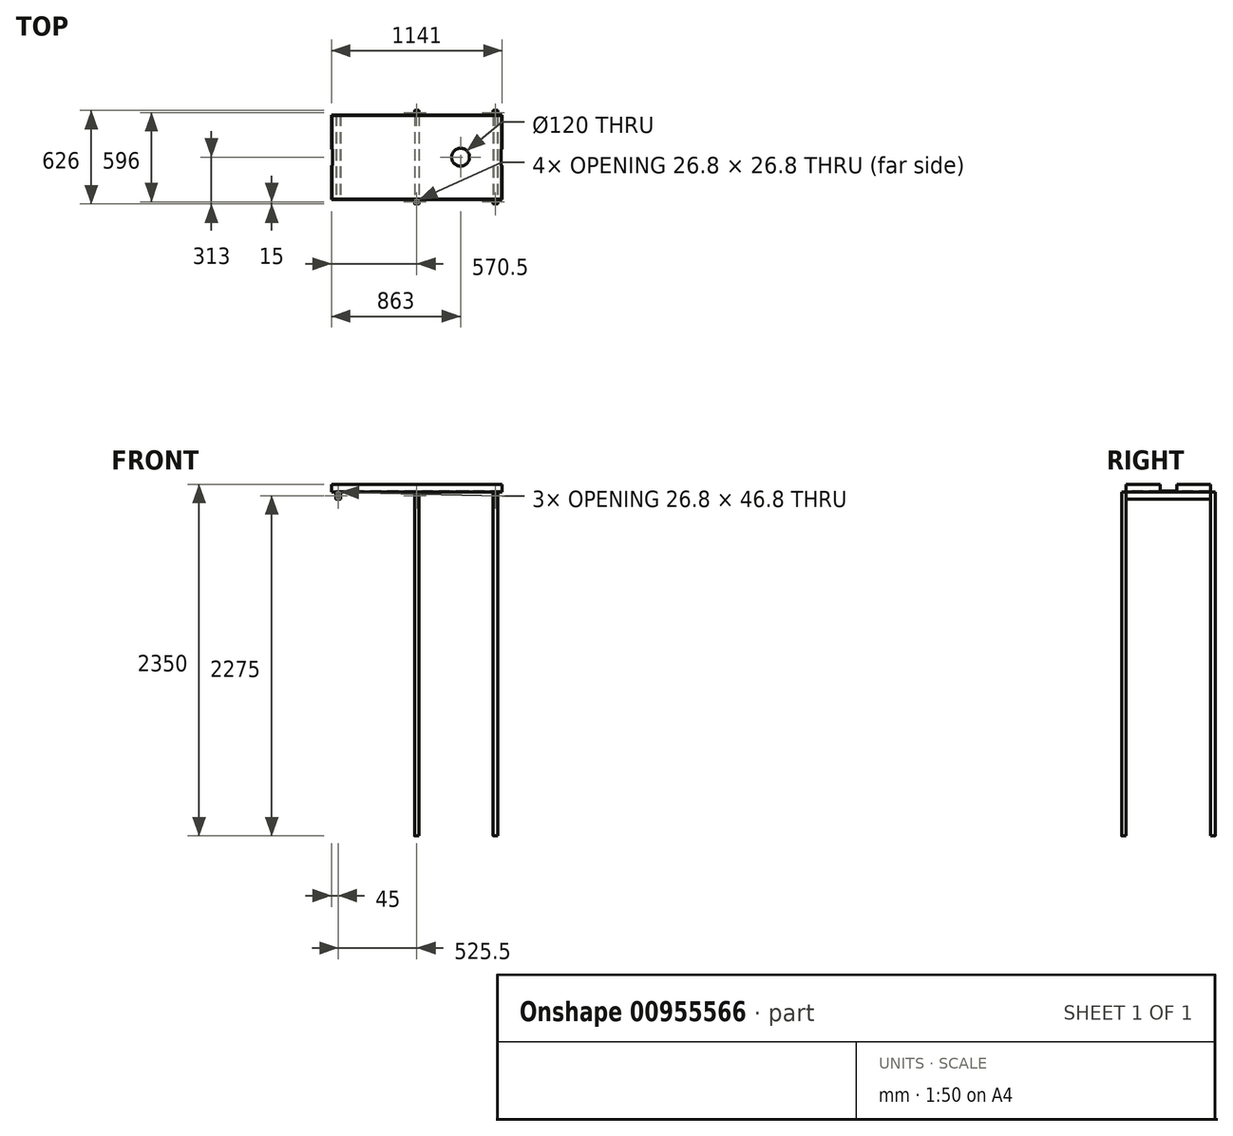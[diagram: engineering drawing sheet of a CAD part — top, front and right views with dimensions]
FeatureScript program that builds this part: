
annotation { "Feature Type Name" : "Feature", "Feature Type Description" : "" }
export const myFeature = defineFeature(function(context is Context, id is Id, definition is map)
    precondition{}
    {
        {
            var Q0;
            Q0=qCreatedBy(makeId("Top.planeOp"),FACE);
            var sketch = newSketch(context, id + "F0", { "sketchPlane" : qUnion([Q0])});
            skLineSegment(sketch, "E0.bottom", {"start": v(567.5, 280) * mm, "end": v(-567.5, 280) * mm});
            skLineSegment(sketch, "E0.top", {"start": v(567.5, -280) * mm, "end": v(-567.5, -280) * mm});
            skLineSegment(sketch, "E0.left", {"start": v(567.5, 280) * mm, "end": v(567.5, -280) * mm});
            skLineSegment(sketch, "E0.right", {"start": v(-567.5, 280) * mm, "end": v(-567.5, -280) * mm});
            skPoint(sketch, "E0.middle", {"position": v(0, 0) * mm});
            skLineSegment(sketch, "E1.0", {"start": v(570.5, 283) * mm, "end": v(-570.5, 283) * mm});
            skLineSegment(sketch, "E1.1", {"start": v(570.5, 283) * mm, "end": v(570.5, -283) * mm});
            skLineSegment(sketch, "E1.2", {"start": v(570.5, -283) * mm, "end": v(-570.5, -283) * mm});
            skLineSegment(sketch, "E1.3", {"start": v(-570.5, 283) * mm, "end": v(-570.5, -283) * mm});
            skLineSegment(sketch, "E2.bottom", {"start": v(567.5, 55) * mm, "end": v(-567.5, 55) * mm, "construction": true});
            skLineSegment(sketch, "E2.top", {"start": v(567.5, -55) * mm, "end": v(-567.5, -55) * mm, "construction": true});
            skLineSegment(sketch, "E2.left", {"start": v(567.5, 55) * mm, "end": v(567.5, -55) * mm, "construction": true});
            skLineSegment(sketch, "E2.right", {"start": v(-567.5, 55) * mm, "end": v(-567.5, -55) * mm, "construction": true});
            skLineSegment(sketch, "E3.bottom", {"start": v(-567.5, -55) * mm, "end": v(-562.5, -55) * mm});
            skLineSegment(sketch, "E3.top", {"start": v(-567.5, 55) * mm, "end": v(-562.5, 55) * mm});
            skLineSegment(sketch, "E3.left", {"start": v(-567.5, -55) * mm, "end": v(-567.5, 55) * mm});
            skLineSegment(sketch, "E3.right", {"start": v(-562.5, -55) * mm, "end": v(-562.5, 55) * mm});
            skLineSegment(sketch, "E4.MirrorCS", {"start": v(562.5, -55) * mm, "end": v(562.5, 55) * mm});
            skLineSegment(sketch, "E5", {"start": v(-567.5, -55) * mm, "end": v(-570.5, -55) * mm});
            skLineSegment(sketch, "E6", {"start": v(-567.5, 55) * mm, "end": v(-570.5, 55) * mm});
            skLineSegment(sketch, "E7.MirrorCS", {"start": v(567.5, -55) * mm, "end": v(570.5, -55) * mm});
            skLineSegment(sketch, "E8.MirrorCS", {"start": v(567.5, 55) * mm, "end": v(570.5, 55) * mm});
            skLineSegment(sketch, "E9", {"start": v(562.5, -55) * mm, "end": v(567.5, -55) * mm});
            skLineSegment(sketch, "E10", {"start": v(562.5, 55) * mm, "end": v(567.5, 55) * mm});
            skLineSegment(sketch, "E11", {"start": v(-567.5, 0) * mm, "end": v(562.5, 0) * mm, "construction": true});
            skCircle(sketch, "E12", {"center": v(292.5, 0) * mm, "radius": 60 * mm});
            skPoint(sketch, "E13", {"position": v(-540.5, 283) * mm});
            skLineSegment(sketch, "E14.bottom", {"start": v(-538.5, 283) * mm, "end": v(-512.5, 283) * mm});
            skLineSegment(sketch, "E14.top", {"start": v(-538.5, 313) * mm, "end": v(-512.5, 313) * mm});
            skLineSegment(sketch, "E14.left", {"start": v(-540.5, 285) * mm, "end": v(-540.5, 311) * mm});
            skLineSegment(sketch, "E14.right", {"start": v(-510.5, 285) * mm, "end": v(-510.5, 311) * mm});
            skLineSegment(sketch, "E15.0", {"start": v(-538.9, 286.6) * mm, "end": v(-538.9, 309.4) * mm});
            skLineSegment(sketch, "E15.1", {"start": v(-536.9, 311.4) * mm, "end": v(-514.1, 311.4) * mm});
            skLineSegment(sketch, "E15.2", {"start": v(-512.1, 286.6) * mm, "end": v(-512.1, 309.4) * mm});
            skLineSegment(sketch, "E16", {"start": v(-536.9, 284.6) * mm, "end": v(-514.1, 284.6) * mm});
            skPoint(sketch, "E17.visualSharp", {"position": v(-538.9, 311.4) * mm});
            skArc(sketch, "E17.filletArc", {"start": v(-536.9, 311.4) * mm, "mid": v(-538.31, 310.81) * mm, "end": v(-538.9, 309.4) * mm});
            skPoint(sketch, "E18.visualSharp", {"position": v(-512.1, 311.4) * mm});
            skArc(sketch, "E18.filletArc", {"start": v(-512.1, 309.4) * mm, "mid": v(-512.69, 310.81) * mm, "end": v(-514.1, 311.4) * mm});
            skPoint(sketch, "E19.visualSharp", {"position": v(-512.1, 284.6) * mm});
            skArc(sketch, "E19.filletArc", {"start": v(-514.1, 284.6) * mm, "mid": v(-512.69, 285.19) * mm, "end": v(-512.1, 286.6) * mm});
            skPoint(sketch, "E20.visualSharp", {"position": v(-538.9, 284.6) * mm});
            skArc(sketch, "E20.filletArc", {"start": v(-538.9, 286.6) * mm, "mid": v(-538.31, 285.19) * mm, "end": v(-536.9, 284.6) * mm});
            skPoint(sketch, "E21.visualSharp", {"position": v(-540.5, 313) * mm});
            skArc(sketch, "E21.filletArc", {"start": v(-538.5, 313) * mm, "mid": v(-539.91, 312.41) * mm, "end": v(-540.5, 311) * mm});
            skPoint(sketch, "E22.visualSharp", {"position": v(-510.5, 313) * mm});
            skArc(sketch, "E22.filletArc", {"start": v(-510.5, 311) * mm, "mid": v(-511.09, 312.41) * mm, "end": v(-512.5, 313) * mm});
            skPoint(sketch, "E23.visualSharp", {"position": v(-510.5, 283) * mm});
            skArc(sketch, "E23.filletArc", {"start": v(-512.5, 283) * mm, "mid": v(-511.09, 283.59) * mm, "end": v(-510.5, 285) * mm});
            skArc(sketch, "E24.filletArc", {"start": v(-540.5, 285) * mm, "mid": v(-539.91, 283.59) * mm, "end": v(-538.5, 283) * mm});
            skLineSegment(sketch, "E25.MirrorCS", {"start": v(538.5, 313) * mm, "end": v(512.5, 313) * mm});
            skLineSegment(sketch, "E26.MirrorCS", {"start": v(536.9, 311.4) * mm, "end": v(514.1, 311.4) * mm});
            skLineSegment(sketch, "E27.MirrorCS", {"start": v(536.9, 284.6) * mm, "end": v(514.1, 284.6) * mm});
            skLineSegment(sketch, "E28.MirrorCS", {"start": v(510.5, 285) * mm, "end": v(510.5, 311) * mm});
            skLineSegment(sketch, "E29.MirrorCS", {"start": v(512.1, 286.6) * mm, "end": v(512.1, 309.4) * mm});
            skLineSegment(sketch, "E30.MirrorCS", {"start": v(538.9, 286.6) * mm, "end": v(538.9, 309.4) * mm});
            skLineSegment(sketch, "E31.MirrorCS", {"start": v(540.5, 285) * mm, "end": v(540.5, 311) * mm});
            skArc(sketch, "E32.MirrorCS", {"start": v(512.1, 309.4) * mm, "mid": v(512.69, 310.81) * mm, "end": v(514.1, 311.4) * mm});
            skArc(sketch, "E33.MirrorCS", {"start": v(510.5, 311) * mm, "mid": v(511.09, 312.41) * mm, "end": v(512.5, 313) * mm});
            skArc(sketch, "E34.MirrorCS", {"start": v(536.9, 311.4) * mm, "mid": v(538.31, 310.81) * mm, "end": v(538.9, 309.4) * mm});
            skArc(sketch, "E35.MirrorCS", {"start": v(538.5, 313) * mm, "mid": v(539.91, 312.41) * mm, "end": v(540.5, 311) * mm});
            skArc(sketch, "E36.MirrorCS", {"start": v(512.5, 283) * mm, "mid": v(511.09, 283.59) * mm, "end": v(510.5, 285) * mm});
            skArc(sketch, "E37.MirrorCS", {"start": v(514.1, 284.6) * mm, "mid": v(512.69, 285.19) * mm, "end": v(512.1, 286.6) * mm});
            skArc(sketch, "E38.MirrorCS", {"start": v(538.9, 286.6) * mm, "mid": v(538.31, 285.19) * mm, "end": v(536.9, 284.6) * mm});
            skArc(sketch, "E39.MirrorCS", {"start": v(540.5, 285) * mm, "mid": v(539.91, 283.59) * mm, "end": v(538.5, 283) * mm});
            skLineSegment(sketch, "E40.1.0.0", {"start": v(-13, 313) * mm, "end": v(13, 313) * mm});
            skPoint(sketch, "E40.1.0.1", {"position": v(-13.4, 284.6) * mm});
            skLineSegment(sketch, "E40.1.0.2", {"start": v(13.4, 286.6) * mm, "end": v(13.4, 309.4) * mm});
            skLineSegment(sketch, "E40.1.0.3", {"start": v(-13.4, 286.6) * mm, "end": v(-13.4, 309.4) * mm});
            skPoint(sketch, "E40.1.0.4", {"position": v(13.4, 284.6) * mm});
            skPoint(sketch, "E40.1.0.5", {"position": v(-15, 313) * mm});
            skLineSegment(sketch, "E40.1.0.6", {"start": v(-15, 285) * mm, "end": v(-15, 311) * mm});
            skPoint(sketch, "E40.1.0.7", {"position": v(13.4, 311.4) * mm});
            skLineSegment(sketch, "E40.1.0.8", {"start": v(-11.4, 284.6) * mm, "end": v(11.4, 284.6) * mm});
            skPoint(sketch, "E40.1.0.9", {"position": v(15, 313) * mm});
            skLineSegment(sketch, "E40.1.0.10", {"start": v(15, 285) * mm, "end": v(15, 311) * mm});
            skLineSegment(sketch, "E40.1.0.11", {"start": v(-13, 283) * mm, "end": v(13, 283) * mm});
            skLineSegment(sketch, "E40.1.0.12", {"start": v(-11.4, 311.4) * mm, "end": v(11.4, 311.4) * mm});
            skPoint(sketch, "E40.1.0.13", {"position": v(-13.4, 311.4) * mm});
            skArc(sketch, "E40.1.0.14", {"start": v(13.4, 309.4) * mm, "mid": v(12.81, 310.81) * mm, "end": v(11.4, 311.4) * mm});
            skArc(sketch, "E40.1.0.15", {"start": v(15, 311) * mm, "mid": v(14.41, 312.41) * mm, "end": v(13, 313) * mm});
            skArc(sketch, "E40.1.0.16", {"start": v(-13, 313) * mm, "mid": v(-14.41, 312.41) * mm, "end": v(-15, 311) * mm});
            skArc(sketch, "E40.1.0.17", {"start": v(-13.4, 286.6) * mm, "mid": v(-12.81, 285.19) * mm, "end": v(-11.4, 284.6) * mm});
            skArc(sketch, "E40.1.0.18", {"start": v(-15, 285) * mm, "mid": v(-14.41, 283.59) * mm, "end": v(-13, 283) * mm});
            skArc(sketch, "E40.1.0.19", {"start": v(11.4, 284.6) * mm, "mid": v(12.81, 285.19) * mm, "end": v(13.4, 286.6) * mm});
            skArc(sketch, "E40.1.0.20", {"start": v(-11.4, 311.4) * mm, "mid": v(-12.81, 310.81) * mm, "end": v(-13.4, 309.4) * mm});
            skArc(sketch, "E40.1.0.21", {"start": v(13, 283) * mm, "mid": v(14.41, 283.59) * mm, "end": v(15, 285) * mm});
            skLineSegment(sketch, "E40.direction1", {"start": v(-538.5, 283) * mm, "end": v(-13, 283) * mm, "construction": true});
            skPoint(sketch, "E41", {"position": v(525.5, 284.6) * mm});
            skLineSegment(sketch, "E42.bottom", {"start": v(-540.5, 313) * mm, "end": v(-510.5, 313) * mm});
            skLineSegment(sketch, "E42.top", {"start": v(-540.5, 333) * mm, "end": v(-510.5, 333) * mm});
            skLineSegment(sketch, "E42.left", {"start": v(-540.5, 313) * mm, "end": v(-540.5, 333) * mm});
            skLineSegment(sketch, "E42.right", {"start": v(-510.5, 313) * mm, "end": v(-510.5, 333) * mm});
            skLineSegment(sketch, "E43.MirrorCS", {"start": v(540.5, 333) * mm, "end": v(510.5, 333) * mm});
            skLineSegment(sketch, "E44.MirrorCS", {"start": v(510.5, 313) * mm, "end": v(510.5, 333) * mm});
            skLineSegment(sketch, "E45.MirrorCS", {"start": v(540.5, 313) * mm, "end": v(540.5, 333) * mm});
            skLineSegment(sketch, "E46.MirrorCS", {"start": v(540.5, 313) * mm, "end": v(510.5, 313) * mm});
            skLineSegment(sketch, "E47.bottom", {"start": v(-15, 313) * mm, "end": v(15, 313) * mm});
            skLineSegment(sketch, "E47.top", {"start": v(-15, 333) * mm, "end": v(15, 333) * mm});
            skLineSegment(sketch, "E47.left", {"start": v(-15, 313) * mm, "end": v(-15, 333) * mm});
            skLineSegment(sketch, "E47.right", {"start": v(15, 313) * mm, "end": v(15, 333) * mm});
            skSolve(sketch);
        }
        {
            var Q0;
            Q0=makeQuery(id+"F0.imprint","IMPRINT",FACE,{"disambiguationData":[TD([[makeQuery(id+"F0.imprint","IMPRINT",EDGE,{"derivedFrom":sQuery(id+"F0.wireOp",EDGE,"E0.bottom")}),1.0]])]});
            extrude(context, id + "F1", {"entities" : qUnion([Q0]), "depth" : 4 * mm, "offsetDistance" : 25 * mm});
        }
        {
            var Q0;
            Q0=makeQuery(id+"F0.imprint","IMPRINT",FACE,{"disambiguationData":[TD([[makeQuery(id+"F0.imprint","IMPRINT",EDGE,{"derivedFrom":sQuery(id+"F0.wireOp",EDGE,"E0.bottom")}),-1.0]])]});
            var Q1;
            {var subQ4=sQuery(id+"F0.wireOp",EDGE,"E0.top");Q1=makeQuery(id+"F0.imprint","IMPRINT",FACE,{"disambiguationData":[TD([[makeQuery(id+"F0.imprint","IMPRINT",EDGE,{"derivedFrom":subQ4}),1.0]])]});}
            extrude(context, id + "F2", {"entities" : qUnion([Q0, Q1]), "operationType" : NewBodyOperationType.ADD, "depth" : 50 * mm, "offsetDistance" : 25 * mm});
        }
        {
            var Q0;
            Q0=makeQuery(id+"F2.opExtrude","SWEPT_FACE",FACE,{"disambiguationData":[OSD([sQuery(id+"F0.wireOp",EDGE,"E1.2")])]});
            var sketch = newSketch(context, id + "F3", { "sketchPlane" : qUnion([Q0])});
            skPoint(sketch, "E48", {"position": v(-540.5, 0) * mm});
            skLineSegment(sketch, "E49.bottom", {"start": v(-538.5, 0) * mm, "end": v(-512.5, 0) * mm});
            skLineSegment(sketch, "E49.top", {"start": v(-538.5, -50) * mm, "end": v(-512.5, -50) * mm});
            skLineSegment(sketch, "E49.left", {"start": v(-540.5, -2) * mm, "end": v(-540.5, -48) * mm});
            skLineSegment(sketch, "E49.right", {"start": v(-510.5, -2) * mm, "end": v(-510.5, -48) * mm});
            skLineSegment(sketch, "E50.MirrorCS", {"start": v(538.5, -50) * mm, "end": v(512.5, -50) * mm});
            skLineSegment(sketch, "E51.MirrorCS", {"start": v(540.5, -2) * mm, "end": v(540.5, -48) * mm});
            skLineSegment(sketch, "E52.MirrorCS", {"start": v(510.5, -2) * mm, "end": v(510.5, -48) * mm});
            skLineSegment(sketch, "E53.MirrorCS", {"start": v(538.5, 0) * mm, "end": v(512.5, 0) * mm});
            skPoint(sketch, "E54", {"position": v(-15, 0) * mm});
            skLineSegment(sketch, "E55.bottom", {"start": v(-13, 0) * mm, "end": v(13, 0) * mm});
            skLineSegment(sketch, "E55.top", {"start": v(-13, -50) * mm, "end": v(13, -50) * mm});
            skLineSegment(sketch, "E55.left", {"start": v(-15, -2) * mm, "end": v(-15, -48) * mm});
            skLineSegment(sketch, "E55.right", {"start": v(15, -2) * mm, "end": v(15, -48) * mm});
            skPoint(sketch, "E56.visualSharp", {"position": v(-510.5, -50) * mm});
            skArc(sketch, "E56.filletArc", {"start": v(-512.5, -50) * mm, "mid": v(-511.09, -49.41) * mm, "end": v(-510.5, -48) * mm});
            skPoint(sketch, "E57.visualSharp", {"position": v(-540.5, -50) * mm});
            skArc(sketch, "E57.filletArc", {"start": v(-540.5, -48) * mm, "mid": v(-539.91, -49.41) * mm, "end": v(-538.5, -50) * mm});
            skPoint(sketch, "E58.visualSharp", {"position": v(-510.5, 0) * mm});
            skArc(sketch, "E58.filletArc", {"start": v(-510.5, -2) * mm, "mid": v(-511.09, -0.59) * mm, "end": v(-512.5, 0) * mm});
            skArc(sketch, "E59.filletArc", {"start": v(-538.5, 0) * mm, "mid": v(-539.91, -0.59) * mm, "end": v(-540.5, -2) * mm});
            skPoint(sketch, "E60.visualSharp", {"position": v(540.5, 0) * mm});
            skArc(sketch, "E60.filletArc", {"start": v(540.5, -2) * mm, "mid": v(539.91, -0.59) * mm, "end": v(538.5, 0) * mm});
            skPoint(sketch, "E61.visualSharp", {"position": v(510.5, 0) * mm});
            skArc(sketch, "E61.filletArc", {"start": v(512.5, 0) * mm, "mid": v(511.09, -0.59) * mm, "end": v(510.5, -2) * mm});
            skPoint(sketch, "E62.visualSharp", {"position": v(510.5, -50) * mm});
            skArc(sketch, "E62.filletArc", {"start": v(510.5, -48) * mm, "mid": v(511.09, -49.41) * mm, "end": v(512.5, -50) * mm});
            skPoint(sketch, "E63.visualSharp", {"position": v(540.5, -50) * mm});
            skArc(sketch, "E63.filletArc", {"start": v(538.5, -50) * mm, "mid": v(539.91, -49.41) * mm, "end": v(540.5, -48) * mm});
            skPoint(sketch, "E64.visualSharp", {"position": v(-15, -50) * mm});
            skArc(sketch, "E64.filletArc", {"start": v(-15, -48) * mm, "mid": v(-14.41, -49.41) * mm, "end": v(-13, -50) * mm});
            skPoint(sketch, "E65.visualSharp", {"position": v(15, -50) * mm});
            skArc(sketch, "E65.filletArc", {"start": v(13, -50) * mm, "mid": v(14.41, -49.41) * mm, "end": v(15, -48) * mm});
            skPoint(sketch, "E66.visualSharp", {"position": v(15, 0) * mm});
            skArc(sketch, "E66.filletArc", {"start": v(15, -2) * mm, "mid": v(14.41, -0.59) * mm, "end": v(13, 0) * mm});
            skArc(sketch, "E67.filletArc", {"start": v(-13, 0) * mm, "mid": v(-14.41, -0.59) * mm, "end": v(-15, -2) * mm});
            skLineSegment(sketch, "E68.0", {"start": v(-538.9, -2) * mm, "end": v(-538.9, -48) * mm});
            skArc(sketch, "E69.0", {"start": v(-538.9, -48) * mm, "mid": v(-538.78, -48.28) * mm, "end": v(-538.5, -48.4) * mm});
            skLineSegment(sketch, "E70.0", {"start": v(-538.5, -48.4) * mm, "end": v(-512.5, -48.4) * mm});
            skArc(sketch, "E71.0", {"start": v(-512.5, -48.4) * mm, "mid": v(-512.22, -48.28) * mm, "end": v(-512.1, -48) * mm});
            skLineSegment(sketch, "E72.0", {"start": v(-512.1, -2) * mm, "end": v(-512.1, -48) * mm});
            skArc(sketch, "E73.0", {"start": v(-512.1, -2) * mm, "mid": v(-512.22, -1.72) * mm, "end": v(-512.5, -1.6) * mm});
            skArc(sketch, "E74.0", {"start": v(-538.5, -1.6) * mm, "mid": v(-538.78, -1.72) * mm, "end": v(-538.9, -2) * mm});
            skLineSegment(sketch, "E75.0", {"start": v(-538.5, -1.6) * mm, "end": v(-512.5, -1.6) * mm});
            skLineSegment(sketch, "E76.MirrorCS", {"start": v(538.5, -48.4) * mm, "end": v(512.5, -48.4) * mm});
            skArc(sketch, "E77.MirrorCS", {"start": v(538.9, -48) * mm, "mid": v(538.78, -48.28) * mm, "end": v(538.5, -48.4) * mm});
            skLineSegment(sketch, "E78.MirrorCS", {"start": v(538.9, -2) * mm, "end": v(538.9, -48) * mm});
            skArc(sketch, "E79.MirrorCS", {"start": v(512.5, -48.4) * mm, "mid": v(512.22, -48.28) * mm, "end": v(512.1, -48) * mm});
            skLineSegment(sketch, "E80.MirrorCS", {"start": v(512.1, -2) * mm, "end": v(512.1, -48) * mm});
            skArc(sketch, "E81.MirrorCS", {"start": v(512.1, -2) * mm, "mid": v(512.22, -1.72) * mm, "end": v(512.5, -1.6) * mm});
            skLineSegment(sketch, "E82.MirrorCS", {"start": v(538.5, -1.6) * mm, "end": v(512.5, -1.6) * mm});
            skArc(sketch, "E83.MirrorCS", {"start": v(538.5, -1.6) * mm, "mid": v(538.78, -1.72) * mm, "end": v(538.9, -2) * mm});
            skLineSegment(sketch, "E84.0", {"start": v(-13.4, -2) * mm, "end": v(-13.4, -48) * mm});
            skLineSegment(sketch, "E85.0", {"start": v(-13, -1.6) * mm, "end": v(13, -1.6) * mm});
            skLineSegment(sketch, "E86.0", {"start": v(13.4, -2) * mm, "end": v(13.4, -48) * mm});
            skLineSegment(sketch, "E87.0", {"start": v(-13, -48.4) * mm, "end": v(13, -48.4) * mm});
            skArc(sketch, "E88.0", {"start": v(-13.4, -48) * mm, "mid": v(-13.28, -48.28) * mm, "end": v(-13, -48.4) * mm});
            skArc(sketch, "E89.0", {"start": v(13, -48.4) * mm, "mid": v(13.28, -48.28) * mm, "end": v(13.4, -48) * mm});
            skArc(sketch, "E90.0", {"start": v(13.4, -2) * mm, "mid": v(13.28, -1.72) * mm, "end": v(13, -1.6) * mm});
            skArc(sketch, "E91.0", {"start": v(-13, -1.6) * mm, "mid": v(-13.28, -1.72) * mm, "end": v(-13.4, -2) * mm});
            skSolve(sketch);
        }
        {
            var Q0;
            Q0=qSketchRegion(id+"F3",true);
            extrude(context, id + "F4", {"entities" : qUnion([Q0]), "oppositeDirection" : true, "depth" : 566 * mm, "offsetDistance" : 25 * mm});
        }
        {
            var Q0;
            Q0=makeQuery(id+"F0.imprint","IMPRINT",FACE,{"disambiguationData":[TD([[makeQuery(id+"F0.imprint","IMPRINT",EDGE,{"derivedFrom":sQuery(id+"F0.wireOp",EDGE,"E14.bottom")}),1.0]])]});
            var Q1;
            Q1=makeQuery(id+"F0.imprint","IMPRINT",FACE,{"disambiguationData":[TD([[makeQuery(id+"F0.imprint","IMPRINT",EDGE,{"derivedFrom":sQuery(id+"F0.wireOp",EDGE,"E40.1.0.2")}),-1.0]])]});
            var Q2;
            Q2=makeQuery(id+"F0.imprint","IMPRINT",FACE,{"disambiguationData":[TD([[makeQuery(id+"F0.imprint","IMPRINT",EDGE,{"derivedFrom":sQuery(id+"F0.wireOp",EDGE,"E26.MirrorCS")}),-1.0]])]});
            extrude(context, id + "F5", {"entities" : qUnion([Q0, Q1, Q2]), "oppositeDirection" : true, "depth" : 2300 * mm, "offsetDistance" : 25 * mm});
        }
        {
            var Q0;
            Q0=makeQuery(id+"F5.opExtrude","SWEPT_BODY",BODY,{"disambiguationData":[OSD([sQuery(id+"F0.wireOp",EDGE,"E14.bottom"),sQuery(id+"F0.wireOp",EDGE,"E14.left"),sQuery(id+"F0.wireOp",EDGE,"E14.right"),sQuery(id+"F0.wireOp",EDGE,"E15.0"),sQuery(id+"F0.wireOp",EDGE,"E15.1"),sQuery(id+"F0.wireOp",EDGE,"E15.2"),sQuery(id+"F0.wireOp",EDGE,"E16"),sQuery(id+"F0.wireOp",EDGE,"E17.filletArc"),sQuery(id+"F0.wireOp",EDGE,"E18.filletArc"),sQuery(id+"F0.wireOp",EDGE,"E19.filletArc"),sQuery(id+"F0.wireOp",EDGE,"E20.filletArc"),sQuery(id+"F0.wireOp",EDGE,"E21.filletArc"),sQuery(id+"F0.wireOp",EDGE,"E22.filletArc"),sQuery(id+"F0.wireOp",EDGE,"E23.filletArc"),sQuery(id+"F0.wireOp",EDGE,"E24.filletArc"),sQuery(id+"F0.wireOp",EDGE,"E42.bottom")])]});
            var Q1;
            Q1=makeQuery(id+"F5.opExtrude","SWEPT_BODY",BODY,{"disambiguationData":[OSD([sQuery(id+"F0.wireOp",EDGE,"E1.0"),sQuery(id+"F0.wireOp",EDGE,"E26.MirrorCS"),sQuery(id+"F0.wireOp",EDGE,"E27.MirrorCS"),sQuery(id+"F0.wireOp",EDGE,"E28.MirrorCS"),sQuery(id+"F0.wireOp",EDGE,"E29.MirrorCS"),sQuery(id+"F0.wireOp",EDGE,"E30.MirrorCS"),sQuery(id+"F0.wireOp",EDGE,"E31.MirrorCS"),sQuery(id+"F0.wireOp",EDGE,"E32.MirrorCS"),sQuery(id+"F0.wireOp",EDGE,"E33.MirrorCS"),sQuery(id+"F0.wireOp",EDGE,"E34.MirrorCS"),sQuery(id+"F0.wireOp",EDGE,"E35.MirrorCS"),sQuery(id+"F0.wireOp",EDGE,"E36.MirrorCS"),sQuery(id+"F0.wireOp",EDGE,"E37.MirrorCS"),sQuery(id+"F0.wireOp",EDGE,"E38.MirrorCS"),sQuery(id+"F0.wireOp",EDGE,"E39.MirrorCS"),sQuery(id+"F0.wireOp",EDGE,"E46.MirrorCS")])]});
            var Q2;
            Q2=makeQuery(id+"F5.opExtrude","SWEPT_BODY",BODY,{"disambiguationData":[OSD([sQuery(id+"F0.wireOp",EDGE,"E40.1.0.2"),sQuery(id+"F0.wireOp",EDGE,"E40.1.0.3"),sQuery(id+"F0.wireOp",EDGE,"E40.1.0.6"),sQuery(id+"F0.wireOp",EDGE,"E40.1.0.8"),sQuery(id+"F0.wireOp",EDGE,"E40.1.0.10"),sQuery(id+"F0.wireOp",EDGE,"E40.1.0.11"),sQuery(id+"F0.wireOp",EDGE,"E40.1.0.12"),sQuery(id+"F0.wireOp",EDGE,"E40.1.0.14"),sQuery(id+"F0.wireOp",EDGE,"E40.1.0.15"),sQuery(id+"F0.wireOp",EDGE,"E40.1.0.16"),sQuery(id+"F0.wireOp",EDGE,"E40.1.0.17"),sQuery(id+"F0.wireOp",EDGE,"E40.1.0.18"),sQuery(id+"F0.wireOp",EDGE,"E40.1.0.19"),sQuery(id+"F0.wireOp",EDGE,"E40.1.0.20"),sQuery(id+"F0.wireOp",EDGE,"E40.1.0.21"),sQuery(id+"F0.wireOp",EDGE,"E47.bottom")])]});
            var Q3;
            Q3=qCreatedBy(makeId("Front.planeOp"),FACE);
            mirror(context, id + "F6", {"entities" : qUnion([Q0, Q1, Q2]), "mirrorPlane" : qUnion([Q3])});
        }
    });
